# Revit family: Paper_Towel_Dispenser_Waste_Receptacle-Bobrick-Classic_Series-B-3947 (2)
name_source: partatom
category: Specialty Equipment
revit_build: Autodesk Revit 2018 (Build: 20170223_1515(x64)
units: mm (PartAtom-declared; Revit-internal decimal feet)

## family parameters
Cut with Voids When Loaded = No
Host = Face
OmniClass Number = 23.40.20.21.17
OmniClass Title = Paper Towel Dispensers, Disposal Units
Part Type = Normal
Room Calculation Point = No
Round Connector Dimension = Use Diameter
Shared = Yes

## types (1)
- B-3947
    367-60 Interchangeable Receptacle, 12-gal. (45.5-L). = No
    368-60 Interchangeable Receptacle = No
    3944-130 Towel Mate = No
    3944-134 Liner Mate = No
    3961-50 Touch-Free, Pull Towel Dispenser Module = No
    3974-250 Convertible Automatic, Universal Roll Paper Towel Dispenser Module Equipped with LED Light. = No
    ADA = Yes
    ADA Compliant = Yes
    Assembly Code = C1030200
    Cabinet Material = Stainless Steel-Bobrick-Satin
    Capacity = 18-gal. (68.0-L)
    Default Elevation = 0"
    Description = Recessed Convertible Paper Towel Dispenser/Waste Receptacle
    Door Material = Stainless Steel-Bobrick-Satin
    Flange Material = Stainless Steel-Bobrick-Satin
    Height = 56"
    Inner Frame Width = 15 3/16"
    Installation Type = Recessed Wall Mounted
    Manufacturer = Bobrick
    Material = Stainless Steel-Bobrick-Satin
    Minimum Recessed Depth = 4"
    Model = B-3947
    Mounting Height = 60"
    Mounting Height Constraint = 59 1/2"
    Paper Towel Dispenser Material = Stainless Steel-Bobrick-Satin
    Product Documentation Link = https://www.bobrick.com
    Product Page URL = https://www.bobrick.com
    Revised Date = 05/16/2022
    Type Comments = Dispenses 600 C-fold or 800 multifold towels.
    URL = https://www.bobrick.com
    Warranty Documentation Link = https://www.bobrick.com
    Width = 17 3/16"

## geometry (parser evidence)
native form markers: Sweep x2
no freeform markers — native parametric forms only
